# Revit family: Cortadora_CA-61_GENERADO
name_source: partatom
category: Equipos especializados
revit_build: Autodesk Revit 2014 (Build: 20131024_2115(x64)
units: mm (PartAtom-declared; Revit-internal decimal feet)

## types (4) — shared parameters
Depth = 420 mm
Fabricante = SAMMIC S.L.
Foodservice Equipment Identifier = Sí
Height = 810 mm
Revision Code = 1
URL = https://www.sammic.com
URL Cutsheet = http://www.sammic.com
Width = 430 mm

## per-type parameters (varying)
| type | Comentarios de tipo | Cycle | FL Amps | Modelo | Phase | Specification by Manufacturer | Volts | Weight in Pounds |
| Vegetable preparation machine CA-61 120/60/1 | High-production commercial Vegetable Processor, up to 1.000 kg/h. | 60 Hz | 4 A | 1050741 | 1 | Single-speed motor block + high-production semi-automatic hopper. | 120 V | 62.8 |
| Vegetable preparation machine CA-62 400/50/3 | High-production vegetable cutter, up to 1000 kg/h. | 50 Hz | 2 A | 1050738 | 3 | Two-speed motor block + high-production semi-automatic hopper. | 400 V | 65 |
| Vegetable preparation machine CA-62 400/60/3 | High-production vegetable cutter, up to 1000 kg/h. | 60 Hz | 2 A | 1050740 | 3 | Two-speed motor block + high-production semi-automatic hopper. | 400 V | 65 |
| Vegetable preparation machine CA-62 220/60/3 | High-production vegetable cutter, up to 1000 kg/h. | 60 Hz | 4 A | 1050744 | 3 | Two-speed motor block + high-production semi-automatic hopper. | 220 V | 65 |

note: column(s) folded — value = type name in every type: Descripción
